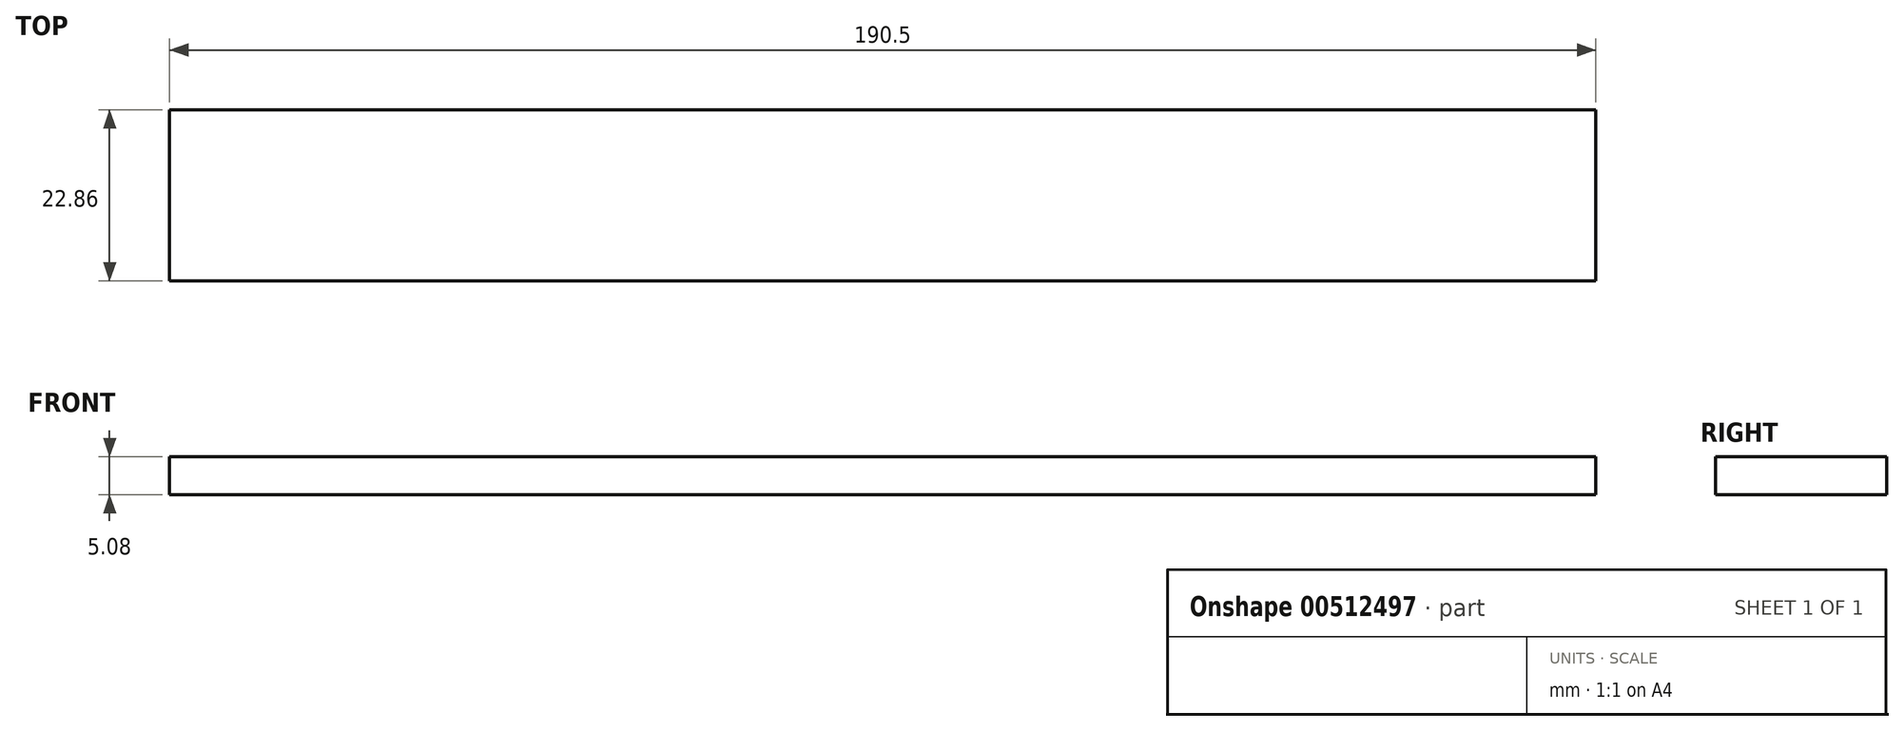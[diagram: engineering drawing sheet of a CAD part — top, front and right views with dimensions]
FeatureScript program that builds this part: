
annotation { "Feature Type Name" : "Feature", "Feature Type Description" : "" }
export const myFeature = defineFeature(function(context is Context, id is Id, definition is map)
    precondition{}
    {
        {
            var Q0;
            Q0=qCreatedBy(makeId("Top.planeOp"),FACE);
            var sketch = newSketch(context, id + "F0", { "sketchPlane" : qUnion([Q0])});
            skLineSegment(sketch, "E0.bottom", {"start": v(-80, 30.94) * mm, "end": v(110.5, 30.94) * mm});
            skLineSegment(sketch, "E0.top", {"start": v(-80, 8.08) * mm, "end": v(110.5, 8.08) * mm});
            skLineSegment(sketch, "E0.left", {"start": v(-80, 30.94) * mm, "end": v(-80, 8.08) * mm});
            skLineSegment(sketch, "E0.right", {"start": v(110.5, 30.94) * mm, "end": v(110.5, 8.08) * mm});
            skSolve(sketch);
        }
        {
            var Q0;
            Q0=makeQuery(id+"F0.imprint","IMPRINT",FACE,{"disambiguationData":[TD([[makeQuery(id+"F0.imprint","IMPRINT",EDGE,{"derivedFrom":sQuery(id+"F0.wireOp",EDGE,"E0.bottom")}),-1.0]])]});
            extrude(context, id + "F1", {"entities" : qUnion([Q0]), "depth" : 5.08 * mm});
        }
    });
